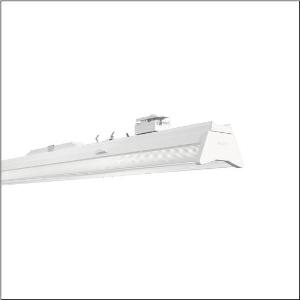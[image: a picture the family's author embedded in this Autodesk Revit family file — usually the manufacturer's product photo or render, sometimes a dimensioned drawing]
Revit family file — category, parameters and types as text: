
# Revit family: licross_r__21_performance_mo_52tm16cn445g_ee6e
name_source: partatom
category: Lighting Fixtures
units: mm (PartAtom-declared; Revit-internal decimal feet)

## family parameters
Cut with Voids When Loaded = No
Host = Face
Light Source = No
Part Type = Normal
Room Calculation Point = No
Round Connector Dimension = Use Diameter
Shared = No

## types (1)
- --- (1 x LED, 4500 lm, 24.1 W, 4000K)
    Apparent Load = 24 VA
    CIE Flux Codes = 66 88 96 79 100
    Color Rendering = 80
    Color Temperature = 4000K
    Default Elevation = 1800 mm
    Description = Licross® 21 Performance MO, luminaire insert, of sheet steel, galvanised, coil coated, white, length: 1.500mm, width: 120mm, height: 123mm, LED rated luminous flux: 4.500lm, light colour: 840, control gear: ON/OFF Multilumen, CLOi, control gear: ECG Multilumen, with plug, 3-pole, with phase selection, mains connection: 220..240V, AC, 50/60Hz, start of lifetime: 24W, end of service life: 28W, halogen-free wiring, primary light control with lens, of plastic, primary optical cover: cover, of PMMA, CAT 2 (L<= 3000cd/m²), light emission: direct/indirect distribution, primary light characteristic: symmetric, protection rating (complete): IP40, insulation class (complete): insulation class I (protective earthing), certification: CE, ENEC, UKCA, protection symbol: D if used in an environment without relevant dust loads with corresponding accessories, impact resistance: IK06, permissible ambient temperature for indoor applications: -35..+55°C, corresponds to IFS (International Featured Standards) requirements for safety and quality in the food industry, reducing of maximum allowable ambient temperature of 5°C with ceiling mounting, LABS conformity tested according to VDMA 24364:2018-05, packaging unit: 1 piece
    Height = 114 mm
    Lamp = 1 x LED
    Lamp Light Flux = 4500 lm
    Lamp Power = 24.1 W
    Lamp count = 1
    Length = 1500 mm
    Luminous efficacy = 187 lm/W
    Manufacturer = Siteco
    ModVariant = No
    Model = 52TM16CN445G
    Mounting Place = Ceiling
    Mounting Type = Pendant
    Number of Poles = 1
    OnlyDefault = Yes
    Power Factor = 1
    Product Name = Licross® 21 Performance MO
    Product group = luminaire insert
    ProductGroupID = 901
    Protection Class = Protection class I
    Protection Degree = IP 40
    RLX_Detail_Level = 1
    RLX_Emergency_Light_Flux = 0 lm
    RLX_Emergency_Type = 0
    RLX_Emergency_Type_DB = No
    RlxData = <blob elided: 31469 chars, md5=db7b66c7>
    Socket = socket
    Standby Power = 0 W
    System Light Flux = 4500 lm
    System Power = 24 W
    Type Comments = factory setting: luminous flux: 100 % | (A | C | E) | 55 mA
    Type Image = l_1256138.jpg
    URL = http://relux.com
    VarID = @adj_015969
    Voltage = 0 V
    Weight = 0.00 kg
    Width = 120 mm

## geometry (parser evidence)
native form markers: Blend x4, Sweep x13
no freeform markers — native parametric forms only
